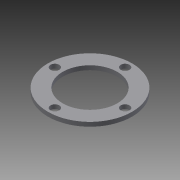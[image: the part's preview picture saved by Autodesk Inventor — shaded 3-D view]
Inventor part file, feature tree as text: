
AUTODESK INVENTOR PART (.ipt)
format: ipt  version: 2013 (Build 170138000, 138)  size: 96,768 bytes
history: native  units: in
note: dims shown in document units (in); Inventor stores cm internally (conversion verified against a paired STEP export)
features: sheet_metal_op x1, sketch x1, other x1
ambient origin geometry x8: Origin, YZ Plane, XZ Plane, XY Plane, X Axis, Y Axis, Z Axis, Center Point
bodies: Solid1 (feature_tree)
feature tree (3):
  sheet_metal_op  "Face1"
  sketch  "Sketch1"  dims[d0=2.09in d1=0.26in d2=0.26in d3=0.26in d4=0.26in d5=1.625in d6=2.5in d7=0.125in]
  other  "Plate1"
